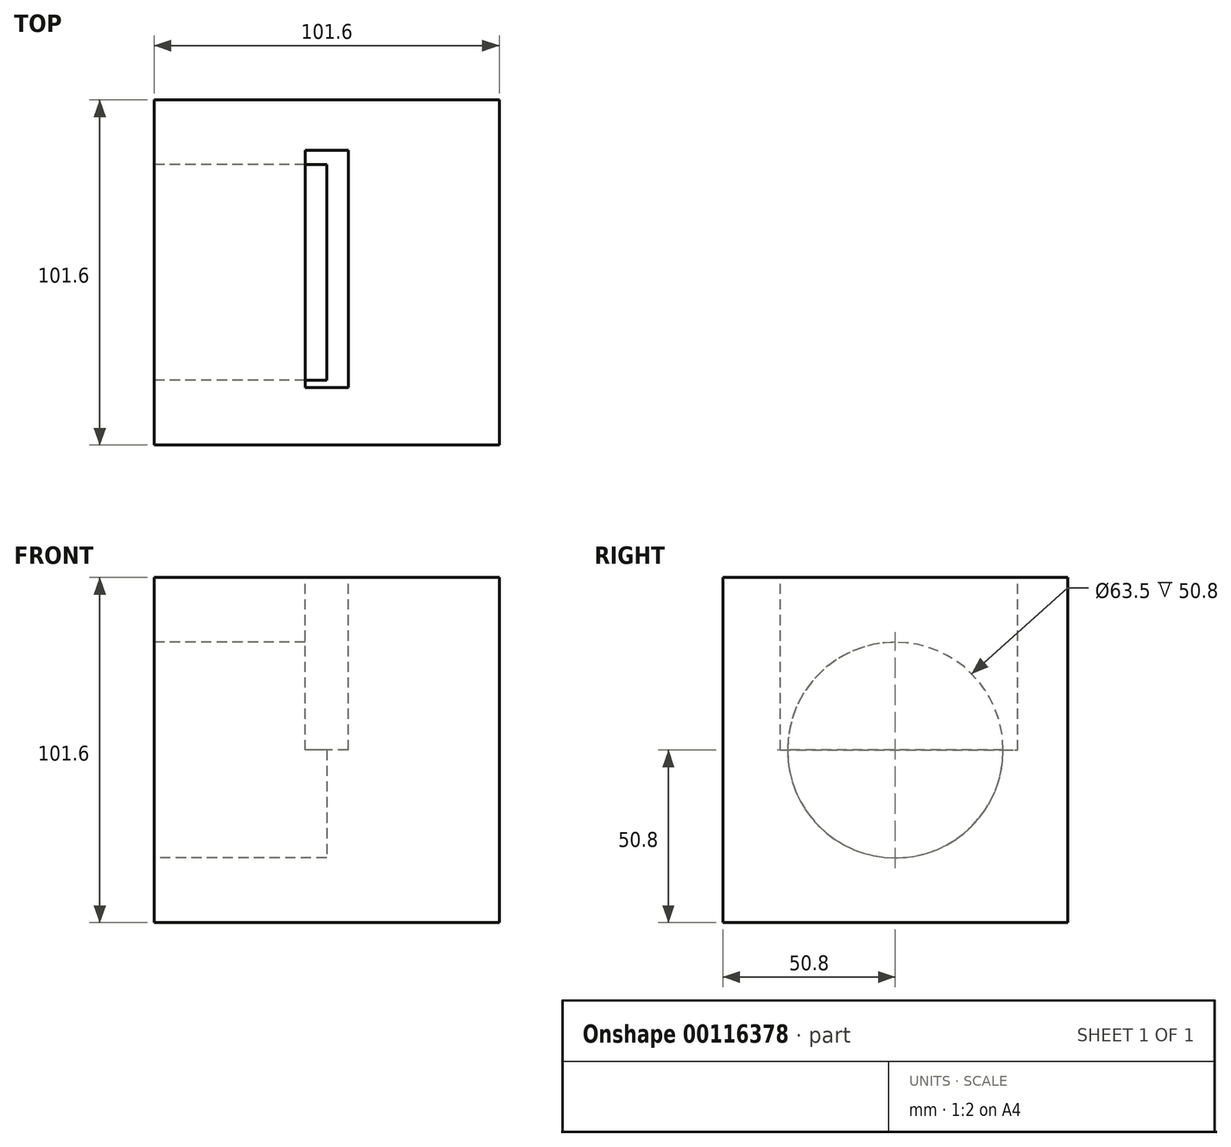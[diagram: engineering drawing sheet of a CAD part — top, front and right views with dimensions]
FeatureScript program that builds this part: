
annotation { "Feature Type Name" : "Feature", "Feature Type Description" : "" }
export const myFeature = defineFeature(function(context is Context, id is Id, definition is map)
    precondition{}
    {
        {
            var Q0;
            Q0=qCreatedBy(makeId("Top.planeOp"),FACE);
            var sketch = newSketch(context, id + "F0", { "sketchPlane" : qUnion([Q0])});
            skLineSegment(sketch, "E0.bottom", {"start": v(50.8, -50.8) * mm, "end": v(-50.8, -50.8) * mm});
            skLineSegment(sketch, "E0.top", {"start": v(50.8, 50.8) * mm, "end": v(-50.8, 50.8) * mm});
            skLineSegment(sketch, "E0.left", {"start": v(50.8, -50.8) * mm, "end": v(50.8, 50.8) * mm});
            skLineSegment(sketch, "E0.right", {"start": v(-50.8, -50.8) * mm, "end": v(-50.8, 50.8) * mm});
            skPoint(sketch, "E0.middle", {"position": v(0, 0) * mm});
            skSolve(sketch);
        }
        {
            var Q0;
            Q0 = qSketchRegion(id + "F0", true);
            extrude(context, id + "F1", {"entities" : qUnion([Q0]), "endBound" : BoundingType.SYMMETRIC, "depth" : 101.6 * mm});
        }
        {
            var Q0;
            Q0=makeQuery(id+"F1.opExtrude","CAP_FACE",FACE,{"disambiguationData":[OSD([sQuery(id+"F0.wireOp",EDGE,"E0.bottom"),sQuery(id+"F0.wireOp",EDGE,"E0.top"),sQuery(id+"F0.wireOp",EDGE,"E0.left"),sQuery(id+"F0.wireOp",EDGE,"E0.right")])],"isStart":false});
            var sketch = newSketch(context, id + "F2", { "sketchPlane" : qUnion([Q0])});
            skLineSegment(sketch, "E1.bottom", {"start": v(6.35, -33.82) * mm, "end": v(-6.35, -33.82) * mm});
            skLineSegment(sketch, "E1.top", {"start": v(6.35, 36.03) * mm, "end": v(-6.35, 36.03) * mm});
            skLineSegment(sketch, "E1.left", {"start": v(6.35, -33.82) * mm, "end": v(6.35, 36.03) * mm});
            skLineSegment(sketch, "E1.right", {"start": v(-6.35, -33.82) * mm, "end": v(-6.35, 36.03) * mm});
            skPoint(sketch, "E1.middle", {"position": v(0, 1.1) * mm});
            skSolve(sketch);
        }
        {
            var Q0;
            Q0 = qSketchRegion(id + "F2", true);
            extrude(context, id + "F3", {"entities" : qUnion([Q0]), "operationType" : NewBodyOperationType.REMOVE, "oppositeDirection" : true, "depth" : 50.8 * mm});
        }
        {
            var Q0;
            Q0=makeQuery(id+"F1.opExtrude","SWEPT_FACE",FACE,{"disambiguationData":[OSD([sQuery(id+"F0.wireOp",EDGE,"E0.right")])]});
            var sketch = newSketch(context, id + "F4", { "sketchPlane" : qUnion([Q0])});
            skCircle(sketch, "E2", {"center": v(0, 0) * mm, "radius": 31.75 * mm});
            skSolve(sketch);
        }
        {
            var Q0;
            Q0=makeQuery(id+"F4.imprint","IMPRINT",FACE,{"disambiguationData":[TD([[makeQuery(id+"F4.imprint","IMPRINT",EDGE,{"derivedFrom":sQuery(id+"F4.wireOp",EDGE,"E2")}),1.0]])]});
            extrude(context, id + "F5", {"entities" : qUnion([Q0]), "operationType" : NewBodyOperationType.REMOVE, "oppositeDirection" : true, "depth" : 50.8 * mm});
        }
    });
